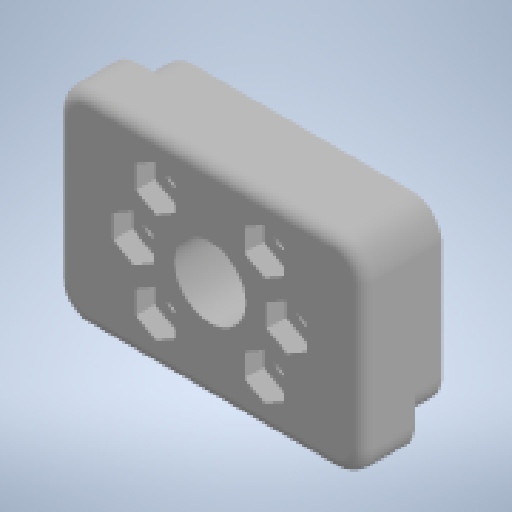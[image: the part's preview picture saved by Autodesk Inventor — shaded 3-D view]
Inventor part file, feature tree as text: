
AUTODESK INVENTOR PART (.ipt)
format: ipt  version: 2023 (Build 270158000, 158)  size: 269,312 bytes
history: native  units: in
note: dims shown in document units (in); Inventor stores cm internally (conversion verified against a paired STEP export)
features: sketch x5, extrude x4, projected_geometry x2, fillet x1, chamfer x1, plane x1
ambient origin geometry x8: Origin, YZ Plane, XZ Plane, XY Plane, X Axis, Y Axis, Z Axis, Center Point
bodies: Solid1 (feature_tree)
feature tree (14):
  extrude  "Extrusion1"  Depth=1.725in
  extrude  "Extrusion2"  Depth=0.3543in TaperAngle=0.0deg
  fillet  "Fillet1"  Radius=3.0in
  extrude  "Extrusion3"  Depth=0.3in
  chamfer  "Chamfer1"  Distance=0.5in
  sketch  "Sketch4"  dims[d10=0.125in d11=0.689in]
  plane  "Work Plane1"
  extrude  "Extrusion6"  Depth=0.125in
  sketch  "Sketch1"  dims[d0=2.725in d1=1.725in]
  sketch  "Sketch2"  dims[d2=0.3in d3=0.3543in d4=0.0in d5=3.0in]
  sketch  "Sketch3"  dims[d6=2.0in d7=0.3in d8=0.5in d9=0.0in]
  projected_geometry  "Projected Loop1"
  projected_geometry  "Projected Loop2"
  sketch  "Sketch7"  dims[d12=0.5in d13=0.0in d14=0.1772in d15=1.4961in d16=45.0deg d17=0.05in d18=0.125in d19=45.0deg d26=0.39in d28=0.1875in d29=0.0in]
